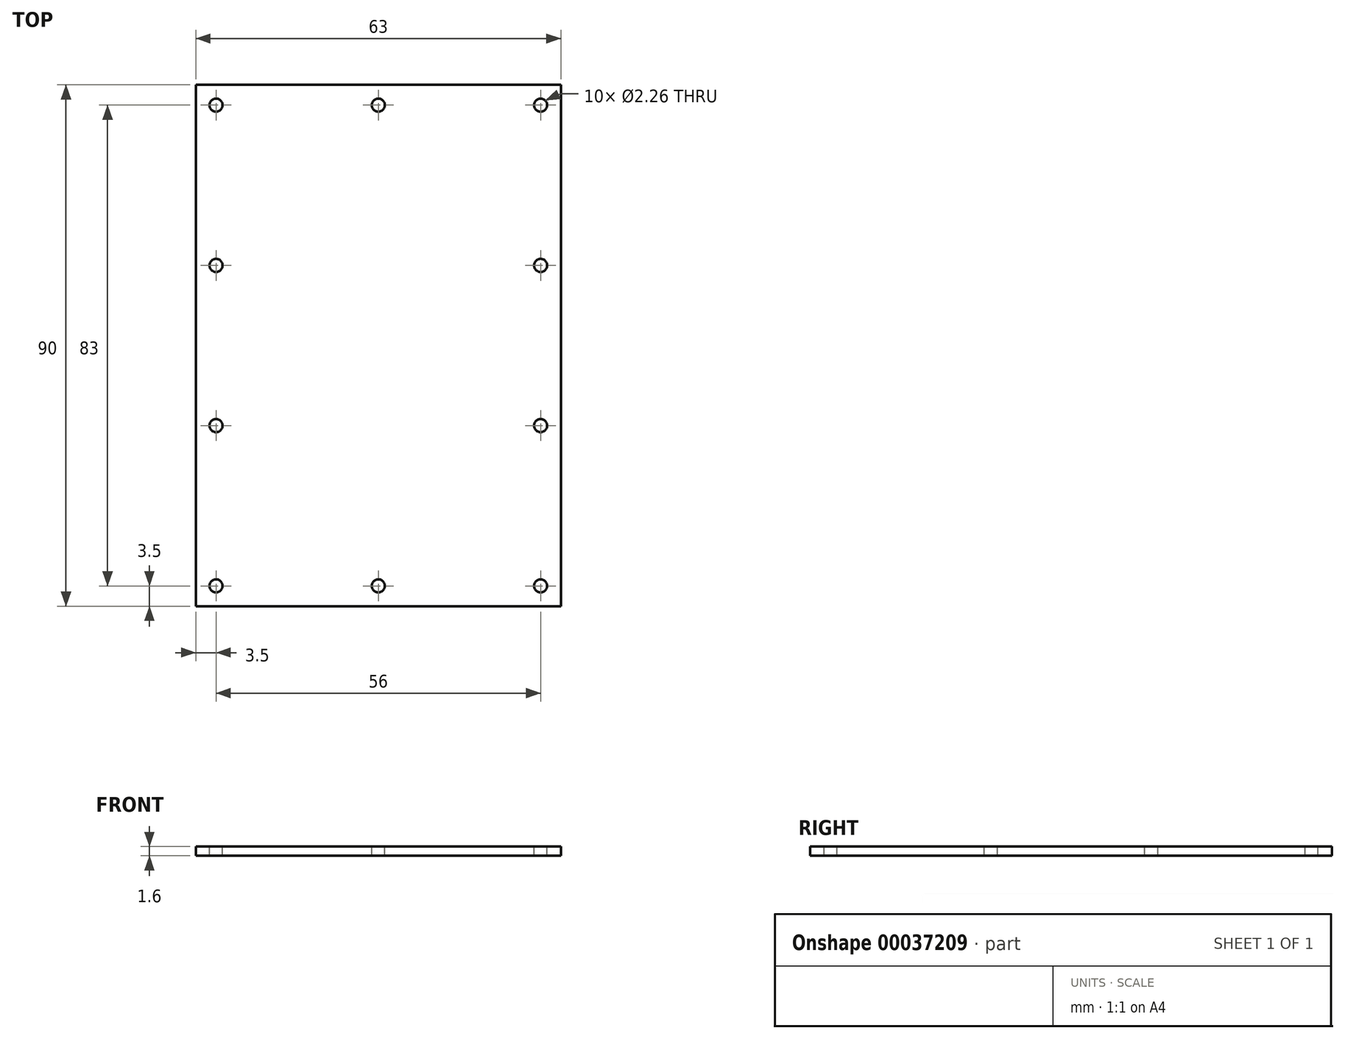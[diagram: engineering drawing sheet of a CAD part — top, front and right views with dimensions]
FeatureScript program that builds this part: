
annotation { "Feature Type Name" : "Feature", "Feature Type Description" : "" }
export const myFeature = defineFeature(function(context is Context, id is Id, definition is map)
    precondition{}
    {
        {
            var Q0;
            Q0=qCreatedBy(makeId("Top.planeOp"),FACE);
            var sketch = newSketch(context, id + "F0", { "sketchPlane" : qUnion([Q0])});
            skLineSegment(sketch, "E0.rect.bottom", {"start": v(31.5, 45) * mm, "end": v(-31.5, 45) * mm});
            skLineSegment(sketch, "E0.rect.top", {"start": v(31.5, -45) * mm, "end": v(-31.5, -45) * mm});
            skLineSegment(sketch, "E0.rect.left", {"start": v(31.5, 45) * mm, "end": v(31.5, -45) * mm});
            skLineSegment(sketch, "E0.rect.right", {"start": v(-31.5, 45) * mm, "end": v(-31.5, -45) * mm});
            skPoint(sketch, "E0.rect.middle", {"position": v(0, 0) * mm});
            skSolve(sketch);
        }
        {
            var Q0;
            Q0=makeQuery(id+"F0.imprint","IMPRINT",FACE,{"disambiguationData":[TD([[makeQuery(id+"F0.imprint","IMPRINT",EDGE,{"derivedFrom":sQuery(id+"F0.wireOp",EDGE,"E0.rect.bottom")}),1.0]])]});
            extrude(context, id + "F1", {"entities" : qUnion([Q0]), "depth" : 1.6 * mm});
        }
        {
            var Q0;
            Q0=makeQuery(id+"F1.opExtrude","CAP_FACE",FACE,{"disambiguationData":[OSD([sQuery(id+"F0.wireOp",EDGE,"E0.rect.bottom"),sQuery(id+"F0.wireOp",EDGE,"E0.rect.top"),sQuery(id+"F0.wireOp",EDGE,"E0.rect.left"),sQuery(id+"F0.wireOp",EDGE,"E0.rect.right")])],"isStart":false});
            var sketch = newSketch(context, id + "F2", { "sketchPlane" : qUnion([Q0])});
            skLineSegment(sketch, "E1.rect.bottom", {"start": v(28, 41.5) * mm, "end": v(-28, 41.5) * mm, "construction": true});
            skLineSegment(sketch, "E1.rect.top", {"start": v(28, -41.5) * mm, "end": v(-28, -41.5) * mm, "construction": true});
            skLineSegment(sketch, "E1.rect.left", {"start": v(28, 41.5) * mm, "end": v(28, -41.5) * mm, "construction": true});
            skLineSegment(sketch, "E1.rect.right", {"start": v(-28, 41.5) * mm, "end": v(-28, -41.5) * mm, "construction": true});
            skPoint(sketch, "E1.rect.middle", {"position": v(0, 0) * mm});
            skPoint(sketch, "E2", {"position": v(0, 41.5) * mm});
            skPoint(sketch, "E3", {"position": v(0, -41.5) * mm});
            skPoint(sketch, "E4", {"position": v(28, 13.83) * mm});
            skPoint(sketch, "E5", {"position": v(28, -13.83) * mm});
            skPoint(sketch, "E6", {"position": v(-28, -13.83) * mm});
            skPoint(sketch, "E7", {"position": v(-28, 13.83) * mm});
            skCircle(sketch, "E8", {"center": v(-28, 41.5) * mm, "radius": 1.13 * mm});
            skCircle(sketch, "E9", {"center": v(0, 41.5) * mm, "radius": 1.13 * mm});
            skCircle(sketch, "E10", {"center": v(28, 41.5) * mm, "radius": 1.13 * mm});
            skCircle(sketch, "E11", {"center": v(28, 13.83) * mm, "radius": 1.13 * mm});
            skCircle(sketch, "E12", {"center": v(28, -13.83) * mm, "radius": 1.13 * mm});
            skCircle(sketch, "E13", {"center": v(0, -41.5) * mm, "radius": 1.13 * mm});
            skCircle(sketch, "E14", {"center": v(-28, -41.5) * mm, "radius": 1.13 * mm});
            skCircle(sketch, "E15", {"center": v(-28, -13.83) * mm, "radius": 1.13 * mm});
            skCircle(sketch, "E16", {"center": v(-28, 13.83) * mm, "radius": 1.13 * mm});
            skCircle(sketch, "E17", {"center": v(28, -41.5) * mm, "radius": 1.13 * mm});
            skSolve(sketch);
        }
        {
            var Q0;
            Q0 = qSketchRegion(id + "F2", true);
            extrude(context, id + "F3", {"entities" : qUnion([Q0]), "operationType" : NewBodyOperationType.REMOVE, "oppositeDirection" : true, "depth" : 25 * mm});
        }
    });
